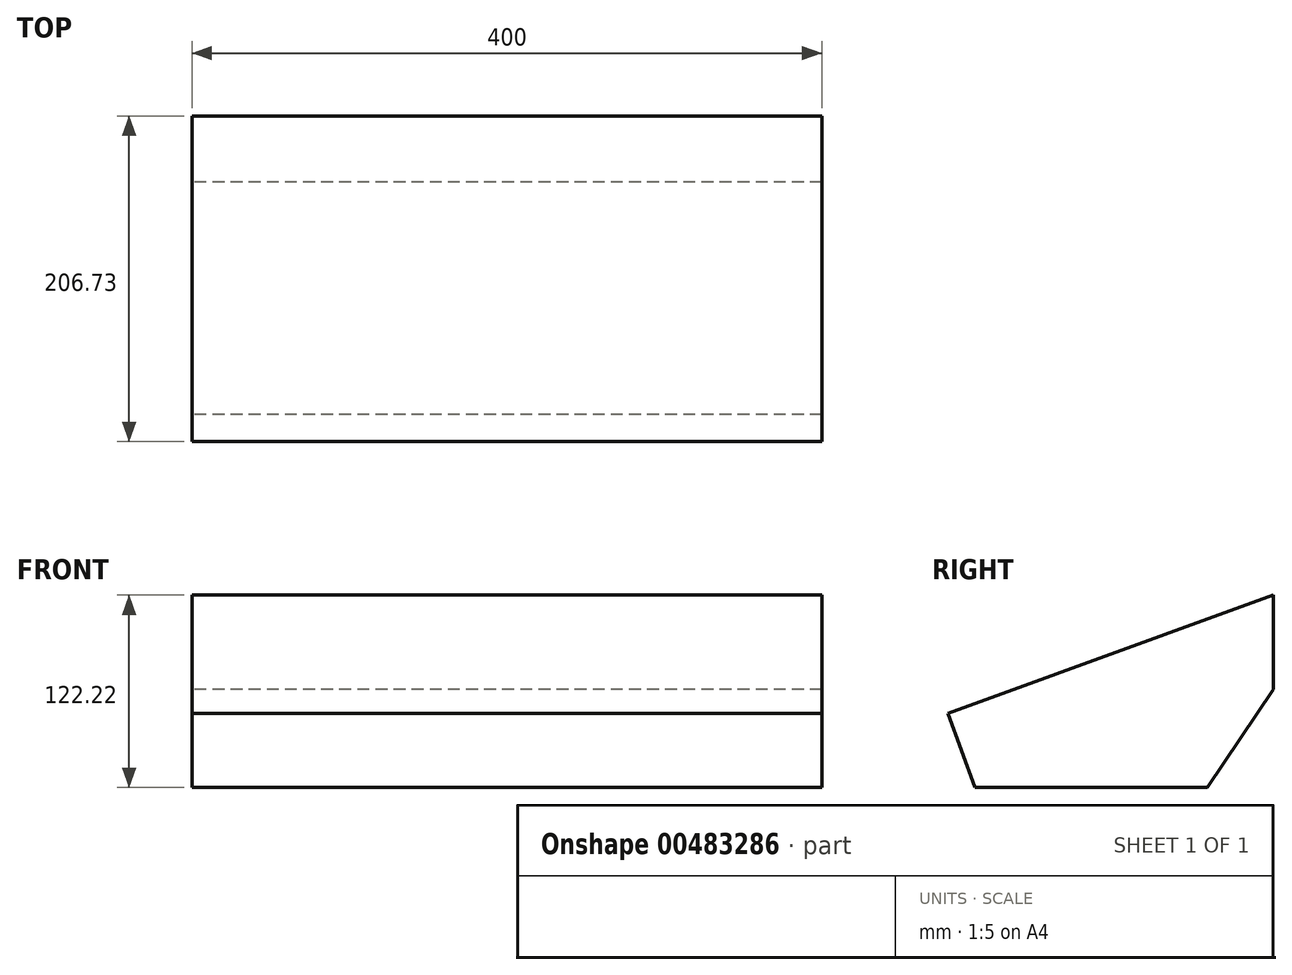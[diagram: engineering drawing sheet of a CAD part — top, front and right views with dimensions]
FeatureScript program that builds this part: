
annotation { "Feature Type Name" : "Feature", "Feature Type Description" : "" }
export const myFeature = defineFeature(function(context is Context, id is Id, definition is map)
    precondition{}
    {
        {
            var Q0;
            Q0=qCreatedBy(makeId("Right.planeOp"),FACE);
            var sketch = newSketch(context, id + "F0", { "sketchPlane" : qUnion([Q0])});
            skLineSegment(sketch, "E0", {"start": v(-66.5, 0) * mm, "end": v(140.23, 75.24) * mm});
            skLineSegment(sketch, "E1", {"start": v(140.23, 15.24) * mm, "end": v(98.26, -46.98) * mm});
            skLineSegment(sketch, "E2", {"start": v(140.23, 75.24) * mm, "end": v(140.23, 15.24) * mm});
            skLineSegment(sketch, "E3", {"start": v(-66.5, 0) * mm, "end": v(-49.4, -46.98) * mm});
            skLineSegment(sketch, "E4", {"start": v(-49.4, -46.98) * mm, "end": v(98.26, -46.98) * mm});
            skSolve(sketch);
        }
        {
            var Q0;
            Q0=makeQuery(id+"F0.imprint","IMPRINT",FACE,{"disambiguationData":[TD([[makeQuery(id+"F0.imprint","IMPRINT",EDGE,{"derivedFrom":sQuery(id+"F0.wireOp",EDGE,"vrPzw0TB-PHxg-kVzE-N9qx-DRdmJ4r2id8z.bottom")}),1.0]])]});
            var Q1;
            Q1=makeQuery(id+"F0.imprint","IMPRINT",FACE,{"disambiguationData":[TD([[makeQuery(id+"F0.imprint","IMPRINT",EDGE,{"derivedFrom":sQuery(id+"F0.wireOp",EDGE,"E0")}),-1.0]])]});
            extrude(context, id + "F1", {"entities" : qUnion([Q0, Q1]), "depth" : 400 * mm, "offsetDistance" : 25 * mm});
        }
    });
